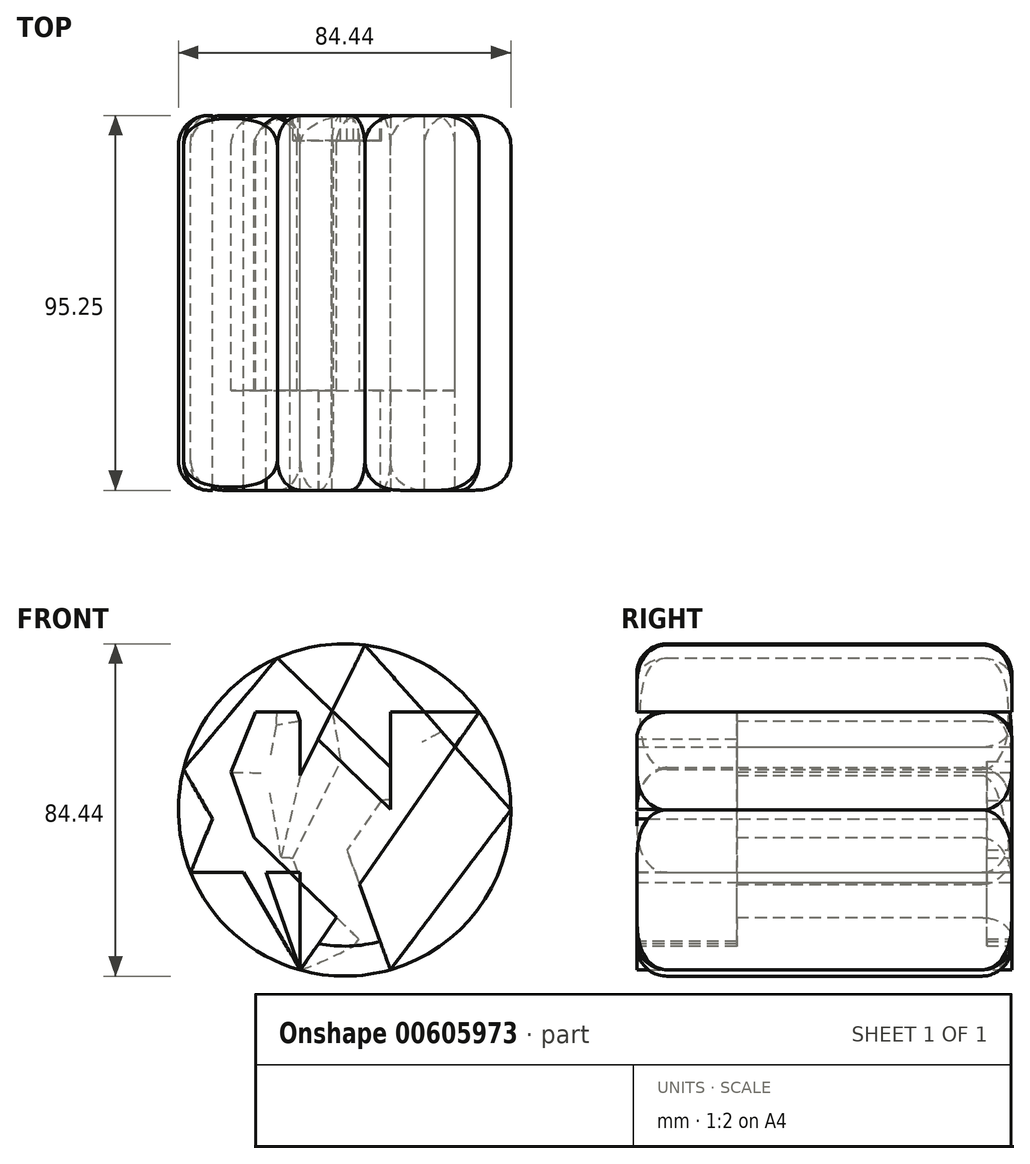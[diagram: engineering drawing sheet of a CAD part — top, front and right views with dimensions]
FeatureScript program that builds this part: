
annotation { "Feature Type Name" : "Feature", "Feature Type Description" : "" }
export const myFeature = defineFeature(function(context is Context, id is Id, definition is map)
    precondition{}
    {
        {
            var Q0;
            Q0=qCreatedBy(makeId("Front.planeOp"),FACE);
            var sketch = newSketch(context, id + "F0", { "sketchPlane" : qUnion([Q0])});
            skCircle(sketch, "E0", {"center": v(0, 0) * mm, "radius": 42.22 * mm});
            skLineSegment(sketch, "E1", {"start": v(-11.28, 40.69) * mm, "end": v(-11.28, -40.69) * mm});
            skLineSegment(sketch, "E2", {"start": v(-11.28, -40.69) * mm, "end": v(-34.14, 24.85) * mm});
            skLineSegment(sketch, "E3", {"start": v(-34.14, 24.85) * mm, "end": v(34.14, 24.85) * mm});
            skLineSegment(sketch, "E4", {"start": v(34.14, 24.85) * mm, "end": v(-11.28, -40.69) * mm});
            skLineSegment(sketch, "E5", {"start": v(11.62, 40.6) * mm, "end": v(11.62, -40.6) * mm});
            skLineSegment(sketch, "E6", {"start": v(11.62, -40.6) * mm, "end": v(-17.09, 38.6) * mm});
            skLineSegment(sketch, "E7", {"start": v(-17.09, 38.6) * mm, "end": v(39.12, -15.88) * mm});
            skLineSegment(sketch, "E8", {"start": v(39.12, -15.88) * mm, "end": v(-39.12, -15.88) * mm});
            skLineSegment(sketch, "E9", {"start": v(-39.12, -15.88) * mm, "end": v(-17.09, 38.6) * mm});
            skLineSegment(sketch, "E10", {"start": v(-30.23, -29.47) * mm, "end": v(5.13, 41.9) * mm});
            skLineSegment(sketch, "E11", {"start": v(5.13, 41.9) * mm, "end": v(42.22, 0) * mm});
            skLineSegment(sketch, "E12", {"start": v(42.22, 0) * mm, "end": v(11.62, -40.6) * mm});
            skLineSegment(sketch, "E13", {"start": v(11.62, -40.6) * mm, "end": v(-40.93, 10.35) * mm});
            skLineSegment(sketch, "E14", {"start": v(-40.93, 10.35) * mm, "end": v(-17.09, 38.6) * mm});
            skLineSegment(sketch, "E15", {"start": v(-40.93, 10.35) * mm, "end": v(-11.28, -40.69) * mm});
            skSolve(sketch);
        }
        {
            var Q0;
            {var subQ0=sQuery(id+"F0.wireOp",EDGE,"E1");var subQ1=sQuery(id+"F0.wireOp",EDGE,"E0");var subQ2=makeQuery(id+"F0.imprint","INTERSECT",VERTEX,{"derivedFrom":[subQ1,subQ0]});Q0=makeQuery(id+"F0.imprint","IMPRINT",FACE,{"disambiguationData":[TD([[makeQuery(id+"F0.imprint","IMPRINT",EDGE,{"disambiguationData":[TD([[subQ2,-1.0]])],"derivedFrom":subQ0}),1.0]])]});}
            var Q1;
            {var subQ0=sQuery(id+"F0.wireOp",EDGE,"E5");var subQ1=sQuery(id+"F0.wireOp",EDGE,"E0");var subQ2=makeQuery(id+"F0.imprint","INTERSECT",VERTEX,{"derivedFrom":[subQ1,subQ0]});Q1=makeQuery(id+"F0.imprint","IMPRINT",FACE,{"disambiguationData":[TD([[makeQuery(id+"F0.imprint","IMPRINT",EDGE,{"disambiguationData":[TD([[subQ2,-1.0]])],"derivedFrom":subQ0}),-1.0]])]});}
            var Q2;
            {var subQ1=sQuery(id+"F0.wireOp",EDGE,"E0");var subQ3=sQuery(id+"F0.wireOp",EDGE,"E5");var subQ4=makeQuery(id+"F0.imprint","INTERSECT",VERTEX,{"derivedFrom":[subQ1,subQ3]});Q2=makeQuery(id+"F0.imprint","IMPRINT",FACE,{"disambiguationData":[TD([[makeQuery(id+"F0.imprint","IMPRINT",EDGE,{"disambiguationData":[TD([[subQ4,-1.0]])],"derivedFrom":subQ3}),1.0]])]});}
            var Q3;
            {var subQ0=sQuery(id+"F0.wireOp",EDGE,"E4");var subQ3=sQuery(id+"F0.wireOp",EDGE,"E11");var subQ5=makeQuery(id+"F0.imprint","INTERSECT",VERTEX,{"derivedFrom":[subQ0,subQ3]});Q3=makeQuery(id+"F0.imprint","IMPRINT",FACE,{"disambiguationData":[TD([[makeQuery(id+"F0.imprint","IMPRINT",EDGE,{"disambiguationData":[TD([[subQ5,1.0]])],"derivedFrom":subQ0}),1.0]])]});}
            var Q4;
            {var subQ0=sQuery(id+"F0.wireOp",EDGE,"E7");var subQ3=sQuery(id+"F0.wireOp",EDGE,"E12");var subQ5=makeQuery(id+"F0.imprint","INTERSECT",VERTEX,{"derivedFrom":[subQ0,subQ3]});Q4=makeQuery(id+"F0.imprint","IMPRINT",FACE,{"disambiguationData":[TD([[makeQuery(id+"F0.imprint","IMPRINT",EDGE,{"disambiguationData":[TD([[subQ5,-1.0]])],"derivedFrom":subQ0}),1.0]])]});}
            var Q5;
            {var subQ1=sQuery(id+"F0.wireOp",EDGE,"E7");var subQ3=sQuery(id+"F0.wireOp",EDGE,"E12");var subQ4=makeQuery(id+"F0.imprint","INTERSECT",VERTEX,{"derivedFrom":[subQ1,subQ3]});Q5=makeQuery(id+"F0.imprint","IMPRINT",FACE,{"disambiguationData":[TD([[makeQuery(id+"F0.imprint","IMPRINT",EDGE,{"disambiguationData":[TD([[subQ4,-1.0]])],"derivedFrom":subQ3}),1.0]])]});}
            var Q6;
            {var subQ0=sQuery(id+"F0.wireOp",EDGE,"E12");var subQ3=sQuery(id+"F0.wireOp",EDGE,"E8");var subQ5=makeQuery(id+"F0.imprint","INTERSECT",VERTEX,{"derivedFrom":[subQ3,subQ0]});Q6=makeQuery(id+"F0.imprint","IMPRINT",FACE,{"disambiguationData":[TD([[makeQuery(id+"F0.imprint","IMPRINT",EDGE,{"disambiguationData":[TD([[subQ5,1.0]])],"derivedFrom":subQ3}),1.0]])]});}
            var Q7;
            {var subQ0=sQuery(id+"F0.wireOp",EDGE,"E4");var subQ3=sQuery(id+"F0.wireOp",EDGE,"E13");var subQ5=makeQuery(id+"F0.imprint","INTERSECT",VERTEX,{"derivedFrom":[subQ0,subQ3]});Q7=makeQuery(id+"F0.imprint","IMPRINT",FACE,{"disambiguationData":[TD([[makeQuery(id+"F0.imprint","IMPRINT",EDGE,{"disambiguationData":[TD([[subQ5,-1.0]])],"derivedFrom":subQ0}),1.0]])]});}
            var Q8;
            {var subQ1=sQuery(id+"F0.wireOp",EDGE,"E0");var subQ3=sQuery(id+"F0.wireOp",EDGE,"E10");var subQ4=makeQuery(id+"F0.imprint","INTERSECT",VERTEX,{"derivedFrom":[subQ1,subQ3]});Q8=makeQuery(id+"F0.imprint","IMPRINT",FACE,{"disambiguationData":[TD([[makeQuery(id+"F0.imprint","IMPRINT",EDGE,{"disambiguationData":[TD([[subQ4,-1.0]])],"derivedFrom":subQ3}),-1.0]])]});}
            var Q9;
            {var subQ1=sQuery(id+"F0.wireOp",EDGE,"E0");var subQ3=sQuery(id+"F0.wireOp",EDGE,"E10");var subQ4=makeQuery(id+"F0.imprint","INTERSECT",VERTEX,{"derivedFrom":[subQ1,subQ3]});Q9=makeQuery(id+"F0.imprint","IMPRINT",FACE,{"disambiguationData":[TD([[makeQuery(id+"F0.imprint","IMPRINT",EDGE,{"disambiguationData":[TD([[subQ4,-1.0]])],"derivedFrom":subQ3}),1.0]])]});}
            var Q10;
            {var subQ0=sQuery(id+"F0.wireOp",EDGE,"E9");var subQ3=sQuery(id+"F0.wireOp",EDGE,"E15");var subQ5=makeQuery(id+"F0.imprint","INTERSECT",VERTEX,{"derivedFrom":[subQ0,subQ3]});Q10=makeQuery(id+"F0.imprint","IMPRINT",FACE,{"disambiguationData":[TD([[makeQuery(id+"F0.imprint","IMPRINT",EDGE,{"disambiguationData":[TD([[subQ5,1.0]])],"derivedFrom":subQ0}),1.0]])]});}
            var Q11;
            {var subQ0=sQuery(id+"F0.wireOp",EDGE,"E2");var subQ3=sQuery(id+"F0.wireOp",EDGE,"E14");var subQ5=makeQuery(id+"F0.imprint","INTERSECT",VERTEX,{"derivedFrom":[subQ0,subQ3]});Q11=makeQuery(id+"F0.imprint","IMPRINT",FACE,{"disambiguationData":[TD([[makeQuery(id+"F0.imprint","IMPRINT",EDGE,{"disambiguationData":[TD([[subQ5,-1.0]])],"derivedFrom":subQ0}),1.0]])]});}
            var Q12;
            {var subQ0=sQuery(id+"F0.wireOp",EDGE,"E1");var subQ1=sQuery(id+"F0.wireOp",EDGE,"E0");var subQ2=makeQuery(id+"F0.imprint","INTERSECT",VERTEX,{"derivedFrom":[subQ1,subQ0]});Q12=makeQuery(id+"F0.imprint","IMPRINT",FACE,{"disambiguationData":[TD([[makeQuery(id+"F0.imprint","IMPRINT",EDGE,{"disambiguationData":[TD([[subQ2,-1.0]])],"derivedFrom":subQ0}),-1.0]])]});}
            var Q13;
            {var subQ1=sQuery(id+"F0.wireOp",EDGE,"E2");var subQ3=sQuery(id+"F0.wireOp",EDGE,"E14");var subQ4=makeQuery(id+"F0.imprint","INTERSECT",VERTEX,{"derivedFrom":[subQ1,subQ3]});Q13=makeQuery(id+"F0.imprint","IMPRINT",FACE,{"disambiguationData":[TD([[makeQuery(id+"F0.imprint","IMPRINT",EDGE,{"disambiguationData":[TD([[subQ4,-1.0]])],"derivedFrom":subQ3}),1.0]])]});}
            var Q14;
            {var subQ0=sQuery(id+"F0.wireOp",EDGE,"E3");var subQ3=sQuery(id+"F0.wireOp",EDGE,"E14");var subQ5=makeQuery(id+"F0.imprint","INTERSECT",VERTEX,{"derivedFrom":[subQ0,subQ3]});Q14=makeQuery(id+"F0.imprint","IMPRINT",FACE,{"disambiguationData":[TD([[makeQuery(id+"F0.imprint","IMPRINT",EDGE,{"disambiguationData":[TD([[subQ5,1.0]])],"derivedFrom":subQ0}),1.0]])]});}
            var Q15;
            {var subQ0=sQuery(id+"F0.wireOp",EDGE,"E10");var subQ1=sQuery(id+"F0.wireOp",EDGE,"E1");var subQ2=makeQuery(id+"F0.imprint","INTERSECT",VERTEX,{"derivedFrom":[subQ1,subQ0]});Q15=makeQuery(id+"F0.imprint","IMPRINT",FACE,{"disambiguationData":[TD([[makeQuery(id+"F0.imprint","IMPRINT",EDGE,{"disambiguationData":[TD([[subQ2,-1.0]])],"derivedFrom":subQ1}),1.0]])]});}
            var Q16;
            {var subQ0=sQuery(id+"F0.wireOp",EDGE,"E10");var subQ1=sQuery(id+"F0.wireOp",EDGE,"E1");var subQ2=makeQuery(id+"F0.imprint","INTERSECT",VERTEX,{"derivedFrom":[subQ1,subQ0]});Q16=makeQuery(id+"F0.imprint","IMPRINT",FACE,{"disambiguationData":[TD([[makeQuery(id+"F0.imprint","IMPRINT",EDGE,{"disambiguationData":[TD([[subQ2,-1.0]])],"derivedFrom":subQ1}),-1.0]])]});}
            var Q17;
            {var subQ0=sQuery(id+"F0.wireOp",EDGE,"E7");var subQ1=sQuery(id+"F0.wireOp",EDGE,"E4");var subQ2=makeQuery(id+"F0.imprint","INTERSECT",VERTEX,{"derivedFrom":[subQ1,subQ0]});Q17=makeQuery(id+"F0.imprint","IMPRINT",FACE,{"disambiguationData":[TD([[makeQuery(id+"F0.imprint","IMPRINT",EDGE,{"disambiguationData":[TD([[subQ2,-1.0]])],"derivedFrom":subQ1}),-1.0]])]});}
            var Q18;
            {var subQ0=sQuery(id+"F0.wireOp",EDGE,"E8");var subQ1=sQuery(id+"F0.wireOp",EDGE,"E4");var subQ2=makeQuery(id+"F0.imprint","INTERSECT",VERTEX,{"derivedFrom":[subQ1,subQ0]});Q18=makeQuery(id+"F0.imprint","IMPRINT",FACE,{"disambiguationData":[TD([[makeQuery(id+"F0.imprint","IMPRINT",EDGE,{"disambiguationData":[TD([[subQ2,-1.0]])],"derivedFrom":subQ1}),-1.0]])]});}
            var Q19;
            {var subQ3=sQuery(id+"F0.wireOp",EDGE,"E10");var subQ11=sQuery(id+"F0.wireOp",EDGE,"E3");var subQ12=makeQuery(id+"F0.imprint","INTERSECT",VERTEX,{"derivedFrom":[subQ11,subQ3]});Q19=makeQuery(id+"F0.imprint","IMPRINT",FACE,{"disambiguationData":[TD([[makeQuery(id+"F0.imprint","IMPRINT",EDGE,{"disambiguationData":[TD([[subQ12,-1.0]])],"derivedFrom":subQ11}),-1.0]])]});}
            var Q20;
            {var subQ0=sQuery(id+"F0.wireOp",EDGE,"E2");var subQ5=sQuery(id+"F0.wireOp",EDGE,"E8");var subQ7=makeQuery(id+"F0.imprint","INTERSECT",VERTEX,{"derivedFrom":[subQ0,subQ5]});Q20=makeQuery(id+"F0.imprint","IMPRINT",FACE,{"disambiguationData":[TD([[makeQuery(id+"F0.imprint","IMPRINT",EDGE,{"disambiguationData":[TD([[subQ7,1.0]])],"derivedFrom":subQ5}),1.0]])]});}
            var Q21;
            {var subQ3=sQuery(id+"F0.wireOp",EDGE,"E8");var subQ6=sQuery(id+"F0.wireOp",EDGE,"E1");var subQ9=makeQuery(id+"F0.imprint","INTERSECT",VERTEX,{"derivedFrom":[subQ6,subQ3]});Q21=makeQuery(id+"F0.imprint","IMPRINT",FACE,{"disambiguationData":[TD([[makeQuery(id+"F0.imprint","IMPRINT",EDGE,{"disambiguationData":[TD([[subQ9,-1.0]])],"derivedFrom":subQ6}),1.0]])]});}
            var Q22;
            {var subQ0=sQuery(id+"F0.wireOp",EDGE,"E6");var subQ1=sQuery(id+"F0.wireOp",EDGE,"E4");var subQ2=makeQuery(id+"F0.imprint","INTERSECT",VERTEX,{"derivedFrom":[subQ1,subQ0]});Q22=makeQuery(id+"F0.imprint","IMPRINT",FACE,{"disambiguationData":[TD([[makeQuery(id+"F0.imprint","IMPRINT",EDGE,{"disambiguationData":[TD([[subQ2,-1.0]])],"derivedFrom":subQ1}),1.0]])]});}
            var Q23;
            {var subQ0=sQuery(id+"F0.wireOp",EDGE,"E5");var subQ1=sQuery(id+"F0.wireOp",EDGE,"E3");var subQ2=makeQuery(id+"F0.imprint","INTERSECT",VERTEX,{"derivedFrom":[subQ1,subQ0]});Q23=makeQuery(id+"F0.imprint","IMPRINT",FACE,{"disambiguationData":[TD([[makeQuery(id+"F0.imprint","IMPRINT",EDGE,{"disambiguationData":[TD([[subQ2,-1.0]])],"derivedFrom":subQ1}),-1.0]])]});}
            var Q24;
            {var subQ0=sQuery(id+"F0.wireOp",EDGE,"E6");var subQ1=sQuery(id+"F0.wireOp",EDGE,"E1");var subQ2=makeQuery(id+"F0.imprint","INTERSECT",VERTEX,{"derivedFrom":[subQ1,subQ0]});Q24=makeQuery(id+"F0.imprint","IMPRINT",FACE,{"disambiguationData":[TD([[makeQuery(id+"F0.imprint","IMPRINT",EDGE,{"disambiguationData":[TD([[subQ2,-1.0]])],"derivedFrom":subQ1}),-1.0]])]});}
            extrude(context, id + "F1", {"entities" : qUnion([Q0, Q1, Q2, Q3, Q4, Q5, Q6, Q7, Q8, Q9, Q10, Q11, Q12, Q13, Q14, Q15, Q16, Q17, Q18, Q19, Q20, Q21, Q22, Q23, Q24]), "depth" : 76.2 * mm, "offsetDistance" : 25.4 * mm, "hasSecondDirection" : true, "secondDirectionOppositeDirection" : true, "secondDirectionDepth" : 19.05 * mm});
        }
        {
            var Q0;
            {var subQ0=sQuery(id+"F0.wireOp",EDGE,"E0");var subQ1=makeQuery(id+"F0.imprint","INTERSECT",VERTEX,{"derivedFrom":[subQ0,sQuery(id+"F0.wireOp",EDGE,"E5")]});Q0=makeQuery(id+"F1.opExtrude","CAP_EDGE",EDGE,{"disambiguationData":[OSD([subQ0]),TDD([makeQuery(id+"F0.imprint","IMPRINT",EDGE,{"disambiguationData":[TD([[subQ1,1.0]])],"derivedFrom":subQ0}),makeQuery(id+"F0.imprint","IMPRINT",EDGE,{"disambiguationData":[TD([[subQ1,-1.0]])],"derivedFrom":subQ0})])],"isStart":false});}
            var Q1;
            {var subQ0=sQuery(id+"F0.wireOp",EDGE,"E0");var subQ1=makeQuery(id+"F0.imprint","INTERSECT",VERTEX,{"derivedFrom":[subQ0,sQuery(id+"F0.wireOp",EDGE,"E1")]});Q1=makeQuery(id+"F1.opExtrude","CAP_EDGE",EDGE,{"disambiguationData":[OSD([subQ0]),TDD([makeQuery(id+"F0.imprint","IMPRINT",EDGE,{"disambiguationData":[TD([[subQ1,1.0]])],"derivedFrom":subQ0}),makeQuery(id+"F0.imprint","IMPRINT",EDGE,{"disambiguationData":[TD([[subQ1,-1.0]])],"derivedFrom":subQ0})])],"isStart":false});}
            var Q2;
            {var subQ0=sQuery(id+"F0.wireOp",EDGE,"E0");var subQ1=makeQuery(id+"F0.imprint","INTERSECT",VERTEX,{"derivedFrom":[subQ0,sQuery(id+"F0.wireOp",EDGE,"E2"),sQuery(id+"F0.wireOp",EDGE,"E3")]});Q2=makeQuery(id+"F1.opExtrude","CAP_EDGE",EDGE,{"disambiguationData":[OSD([subQ0]),TDD([makeQuery(id+"F0.imprint","IMPRINT",EDGE,{"disambiguationData":[TD([[subQ1,1.0]])],"derivedFrom":subQ0}),makeQuery(id+"F0.imprint","IMPRINT",EDGE,{"disambiguationData":[TD([[subQ1,-1.0]])],"derivedFrom":subQ0})])],"isStart":false});}
            var Q3;
            {var subQ0=sQuery(id+"F0.wireOp",EDGE,"E0");Q3=makeQuery(id+"F1.opExtrude","CAP_EDGE",EDGE,{"disambiguationData":[OSD([subQ0]),TDD([makeQuery(id+"F0.imprint","IMPRINT",EDGE,{"disambiguationData":[TD([[makeQuery(id+"F0.imprint","INTERSECT",VERTEX,{"derivedFrom":[subQ0,sQuery(id+"F0.wireOp",EDGE,"E8"),sQuery(id+"F0.wireOp",EDGE,"E9")]}),1.0]])],"derivedFrom":subQ0})])],"isStart":false});}
            var Q4;
            {var subQ0=sQuery(id+"F0.wireOp",EDGE,"E0");var subQ1=makeQuery(id+"F0.imprint","INTERSECT",VERTEX,{"derivedFrom":[subQ0,sQuery(id+"F0.wireOp",EDGE,"E10")]});Q4=makeQuery(id+"F1.opExtrude","CAP_EDGE",EDGE,{"disambiguationData":[OSD([subQ0]),TDD([makeQuery(id+"F0.imprint","IMPRINT",EDGE,{"disambiguationData":[TD([[subQ1,1.0]])],"derivedFrom":subQ0}),makeQuery(id+"F0.imprint","IMPRINT",EDGE,{"disambiguationData":[TD([[subQ1,-1.0]])],"derivedFrom":subQ0})])],"isStart":false});}
            var Q5;
            {var subQ0=sQuery(id+"F0.wireOp",EDGE,"E0");Q5=makeQuery(id+"F1.opExtrude","CAP_EDGE",EDGE,{"disambiguationData":[OSD([subQ0]),TDD([makeQuery(id+"F0.imprint","IMPRINT",EDGE,{"disambiguationData":[TD([[makeQuery(id+"F0.imprint","INTERSECT",VERTEX,{"derivedFrom":[subQ0,sQuery(id+"F0.wireOp",EDGE,"E1"),sQuery(id+"F0.wireOp",EDGE,"E2"),sQuery(id+"F0.wireOp",EDGE,"E4"),sQuery(id+"F0.wireOp",EDGE,"E15")]}),-1.0]])],"derivedFrom":subQ0})])],"isStart":false});}
            var Q6;
            {var subQ0=sQuery(id+"F0.wireOp",EDGE,"E0");var subQ1=makeQuery(id+"F0.imprint","INTERSECT",VERTEX,{"derivedFrom":[subQ0,sQuery(id+"F0.wireOp",EDGE,"E7"),sQuery(id+"F0.wireOp",EDGE,"E8")]});Q6=makeQuery(id+"F1.opExtrude","CAP_EDGE",EDGE,{"disambiguationData":[OSD([subQ0]),TDD([makeQuery(id+"F0.imprint","IMPRINT",EDGE,{"disambiguationData":[TD([[subQ1,1.0]])],"derivedFrom":subQ0}),makeQuery(id+"F0.imprint","IMPRINT",EDGE,{"disambiguationData":[TD([[subQ1,-1.0]])],"derivedFrom":subQ0})])],"isStart":false});}
            var Q7;
            {var subQ0=sQuery(id+"F0.wireOp",EDGE,"E0");Q7=makeQuery(id+"F1.opExtrude","CAP_EDGE",EDGE,{"disambiguationData":[OSD([subQ0]),TDD([makeQuery(id+"F0.imprint","IMPRINT",EDGE,{"disambiguationData":[TD([[makeQuery(id+"F0.imprint","INTERSECT",VERTEX,{"derivedFrom":[subQ0,sQuery(id+"F0.wireOp",EDGE,"E3"),sQuery(id+"F0.wireOp",EDGE,"E4")]}),1.0]])],"derivedFrom":subQ0})])],"isStart":false});}
            var Q8;
            {var subQ0=sQuery(id+"F0.wireOp",EDGE,"E0");var subQ1=makeQuery(id+"F0.imprint","INTERSECT",VERTEX,{"derivedFrom":[subQ0,sQuery(id+"F0.wireOp",EDGE,"E5")]});Q8=makeQuery(id+"F1.opExtrude","CAP_EDGE",EDGE,{"disambiguationData":[OSD([subQ0]),TDD([makeQuery(id+"F0.imprint","IMPRINT",EDGE,{"disambiguationData":[TD([[subQ1,1.0]])],"derivedFrom":subQ0}),makeQuery(id+"F0.imprint","IMPRINT",EDGE,{"disambiguationData":[TD([[subQ1,-1.0]])],"derivedFrom":subQ0})])],"isStart":true});}
            var Q9;
            {var subQ0=sQuery(id+"F0.wireOp",EDGE,"E0");Q9=makeQuery(id+"F1.opExtrude","CAP_EDGE",EDGE,{"disambiguationData":[OSD([subQ0]),TDD([makeQuery(id+"F0.imprint","IMPRINT",EDGE,{"disambiguationData":[TD([[makeQuery(id+"F0.imprint","INTERSECT",VERTEX,{"derivedFrom":[subQ0,sQuery(id+"F0.wireOp",EDGE,"E3"),sQuery(id+"F0.wireOp",EDGE,"E4")]}),1.0]])],"derivedFrom":subQ0})])],"isStart":true});}
            var Q10;
            {var subQ0=sQuery(id+"F0.wireOp",EDGE,"E0");var subQ1=makeQuery(id+"F0.imprint","INTERSECT",VERTEX,{"derivedFrom":[subQ0,sQuery(id+"F0.wireOp",EDGE,"E7"),sQuery(id+"F0.wireOp",EDGE,"E8")]});Q10=makeQuery(id+"F1.opExtrude","CAP_EDGE",EDGE,{"disambiguationData":[OSD([subQ0]),TDD([makeQuery(id+"F0.imprint","IMPRINT",EDGE,{"disambiguationData":[TD([[subQ1,1.0]])],"derivedFrom":subQ0}),makeQuery(id+"F0.imprint","IMPRINT",EDGE,{"disambiguationData":[TD([[subQ1,-1.0]])],"derivedFrom":subQ0})])],"isStart":true});}
            var Q11;
            {var subQ0=sQuery(id+"F0.wireOp",EDGE,"E0");Q11=makeQuery(id+"F1.opExtrude","CAP_EDGE",EDGE,{"disambiguationData":[OSD([subQ0]),TDD([makeQuery(id+"F0.imprint","IMPRINT",EDGE,{"disambiguationData":[TD([[makeQuery(id+"F0.imprint","INTERSECT",VERTEX,{"derivedFrom":[subQ0,sQuery(id+"F0.wireOp",EDGE,"E1"),sQuery(id+"F0.wireOp",EDGE,"E2"),sQuery(id+"F0.wireOp",EDGE,"E4"),sQuery(id+"F0.wireOp",EDGE,"E15")]}),-1.0]])],"derivedFrom":subQ0})])],"isStart":true});}
            var Q12;
            {var subQ0=sQuery(id+"F0.wireOp",EDGE,"E0");Q12=makeQuery(id+"F1.opExtrude","CAP_EDGE",EDGE,{"disambiguationData":[OSD([subQ0]),TDD([makeQuery(id+"F0.imprint","IMPRINT",EDGE,{"disambiguationData":[TD([[makeQuery(id+"F0.imprint","INTERSECT",VERTEX,{"derivedFrom":[subQ0,sQuery(id+"F0.wireOp",EDGE,"E8"),sQuery(id+"F0.wireOp",EDGE,"E9")]}),1.0]])],"derivedFrom":subQ0})])],"isStart":true});}
            var Q13;
            {var subQ0=sQuery(id+"F0.wireOp",EDGE,"E0");var subQ1=makeQuery(id+"F0.imprint","INTERSECT",VERTEX,{"derivedFrom":[subQ0,sQuery(id+"F0.wireOp",EDGE,"E10")]});Q13=makeQuery(id+"F1.opExtrude","CAP_EDGE",EDGE,{"disambiguationData":[OSD([subQ0]),TDD([makeQuery(id+"F0.imprint","IMPRINT",EDGE,{"disambiguationData":[TD([[subQ1,1.0]])],"derivedFrom":subQ0}),makeQuery(id+"F0.imprint","IMPRINT",EDGE,{"disambiguationData":[TD([[subQ1,-1.0]])],"derivedFrom":subQ0})])],"isStart":true});}
            var Q14;
            {var subQ0=sQuery(id+"F0.wireOp",EDGE,"E0");var subQ1=makeQuery(id+"F0.imprint","INTERSECT",VERTEX,{"derivedFrom":[subQ0,sQuery(id+"F0.wireOp",EDGE,"E2"),sQuery(id+"F0.wireOp",EDGE,"E3")]});Q14=makeQuery(id+"F1.opExtrude","CAP_EDGE",EDGE,{"disambiguationData":[OSD([subQ0]),TDD([makeQuery(id+"F0.imprint","IMPRINT",EDGE,{"disambiguationData":[TD([[subQ1,1.0]])],"derivedFrom":subQ0}),makeQuery(id+"F0.imprint","IMPRINT",EDGE,{"disambiguationData":[TD([[subQ1,-1.0]])],"derivedFrom":subQ0})])],"isStart":true});}
            var Q15;
            {var subQ0=sQuery(id+"F0.wireOp",EDGE,"E0");var subQ1=makeQuery(id+"F0.imprint","INTERSECT",VERTEX,{"derivedFrom":[subQ0,sQuery(id+"F0.wireOp",EDGE,"E1")]});Q15=makeQuery(id+"F1.opExtrude","CAP_EDGE",EDGE,{"disambiguationData":[OSD([subQ0]),TDD([makeQuery(id+"F0.imprint","IMPRINT",EDGE,{"disambiguationData":[TD([[subQ1,1.0]])],"derivedFrom":subQ0}),makeQuery(id+"F0.imprint","IMPRINT",EDGE,{"disambiguationData":[TD([[subQ1,-1.0]])],"derivedFrom":subQ0})])],"isStart":true});}
            var Q16;
            {var subQ0=sQuery(id+"F0.wireOp",EDGE,"E7");Q16=makeQuery(id+"F1.opExtrude","CAP_EDGE",EDGE,{"disambiguationData":[OSD([subQ0]),TDD([makeQuery(id+"F0.imprint","IMPRINT",EDGE,{"disambiguationData":[TD([[makeQuery(id+"F0.imprint","INTERSECT",VERTEX,{"derivedFrom":[sQuery(id+"F0.wireOp",EDGE,"E3"),subQ0]}),-1.0]])],"derivedFrom":subQ0})])],"isStart":true});}
            var Q17;
            {var subQ0=sQuery(id+"F0.wireOp",EDGE,"E10");Q17=makeQuery(id+"F1.opExtrude","CAP_EDGE",EDGE,{"disambiguationData":[OSD([subQ0]),TDD([makeQuery(id+"F0.imprint","IMPRINT",EDGE,{"disambiguationData":[TD([[makeQuery(id+"F0.imprint","INTERSECT",VERTEX,{"derivedFrom":[sQuery(id+"F0.wireOp",EDGE,"E1"),subQ0]}),-1.0]])],"derivedFrom":subQ0}),makeQuery(id+"F0.imprint","IMPRINT",EDGE,{"disambiguationData":[TD([[makeQuery(id+"F0.imprint","INTERSECT",VERTEX,{"derivedFrom":[sQuery(id+"F0.wireOp",EDGE,"E3"),subQ0]}),1.0]])],"derivedFrom":subQ0})])],"isStart":true});}
            var Q18;
            {var subQ0=sQuery(id+"F0.wireOp",EDGE,"E1");Q18=makeQuery(id+"F1.opExtrude","CAP_EDGE",EDGE,{"disambiguationData":[OSD([subQ0]),TDD([makeQuery(id+"F0.imprint","IMPRINT",EDGE,{"disambiguationData":[TD([[makeQuery(id+"F0.imprint","INTERSECT",VERTEX,{"derivedFrom":[subQ0,sQuery(id+"F0.wireOp",EDGE,"E6")]}),-1.0]])],"derivedFrom":subQ0})])],"isStart":true});}
            var Q19;
            {var subQ0=sQuery(id+"F0.wireOp",EDGE,"E6");Q19=makeQuery(id+"F1.opExtrude","CAP_EDGE",EDGE,{"disambiguationData":[OSD([subQ0]),TDD([makeQuery(id+"F0.imprint","IMPRINT",EDGE,{"disambiguationData":[TD([[makeQuery(id+"F0.imprint","INTERSECT",VERTEX,{"derivedFrom":[sQuery(id+"F0.wireOp",EDGE,"E1"),subQ0]}),-1.0]])],"derivedFrom":subQ0})])],"isStart":true});}
            var Q20;
            {var subQ0=sQuery(id+"F0.wireOp",EDGE,"E2");Q20=makeQuery(id+"F1.opExtrude","CAP_EDGE",EDGE,{"disambiguationData":[OSD([subQ0]),TDD([makeQuery(id+"F0.imprint","IMPRINT",EDGE,{"disambiguationData":[TD([[makeQuery(id+"F0.imprint","INTERSECT",VERTEX,{"derivedFrom":[subQ0,sQuery(id+"F0.wireOp",EDGE,"E13")]}),-1.0]])],"derivedFrom":subQ0})])],"isStart":true});}
            var Q21;
            {var subQ0=sQuery(id+"F0.wireOp",EDGE,"E9");Q21=makeQuery(id+"F1.opExtrude","CAP_EDGE",EDGE,{"disambiguationData":[OSD([subQ0]),TDD([makeQuery(id+"F0.imprint","IMPRINT",EDGE,{"disambiguationData":[TD([[makeQuery(id+"F0.imprint","INTERSECT",VERTEX,{"derivedFrom":[sQuery(id+"F0.wireOp",EDGE,"E2"),subQ0]}),-1.0]])],"derivedFrom":subQ0})])],"isStart":true});}
            var Q22;
            {var subQ0=sQuery(id+"F0.wireOp",EDGE,"E4");Q22=makeQuery(id+"F1.opExtrude","CAP_EDGE",EDGE,{"disambiguationData":[OSD([subQ0]),TDD([makeQuery(id+"F0.imprint","IMPRINT",EDGE,{"disambiguationData":[TD([[makeQuery(id+"F0.imprint","INTERSECT",VERTEX,{"derivedFrom":[subQ0,sQuery(id+"F0.wireOp",EDGE,"E13")]}),-1.0]])],"derivedFrom":subQ0})])],"isStart":true});}
            var Q23;
            {var subQ0=sQuery(id+"F0.wireOp",EDGE,"E4");var subQ1=makeQuery(id+"F0.imprint","INTERSECT",VERTEX,{"derivedFrom":[subQ0,sQuery(id+"F0.wireOp",EDGE,"E8")]});var subQ2=makeQuery(id+"F0.imprint","INTERSECT",VERTEX,{"derivedFrom":[subQ0,sQuery(id+"F0.wireOp",EDGE,"E5")]});var subQ3=makeQuery(id+"F0.imprint","INTERSECT",VERTEX,{"derivedFrom":[subQ0,sQuery(id+"F0.wireOp",EDGE,"E7")]});Q23=makeQuery(id+"F1.opExtrude","CAP_EDGE",EDGE,{"disambiguationData":[OSD([subQ0]),TDD([makeQuery(id+"F0.imprint","IMPRINT",EDGE,{"disambiguationData":[TD([[makeQuery(id+"F0.imprint","INTERSECT",VERTEX,{"derivedFrom":[subQ0,sQuery(id+"F0.wireOp",EDGE,"E11")]}),-1.0]])],"derivedFrom":subQ0}),makeQuery(id+"F0.imprint","IMPRINT",EDGE,{"disambiguationData":[TD([[subQ3,-1.0]])],"derivedFrom":subQ0}),makeQuery(id+"F0.imprint","IMPRINT",EDGE,{"disambiguationData":[TD([[subQ2,-1.0]])],"derivedFrom":subQ0}),makeQuery(id+"F0.imprint","IMPRINT",EDGE,{"disambiguationData":[TD([[subQ1,-1.0]])],"derivedFrom":subQ0})])],"isStart":true});}
            var Q24;
            {var subQ0=sQuery(id+"F0.wireOp",EDGE,"E3");Q24=makeQuery(id+"F1.opExtrude","CAP_EDGE",EDGE,{"disambiguationData":[OSD([subQ0]),TDD([makeQuery(id+"F0.imprint","IMPRINT",EDGE,{"disambiguationData":[TD([[makeQuery(id+"F0.imprint","INTERSECT",VERTEX,{"derivedFrom":[subQ0,sQuery(id+"F0.wireOp",EDGE,"E5")]}),-1.0]])],"derivedFrom":subQ0})])],"isStart":true});}
            var Q25;
            {var subQ0=sQuery(id+"F0.wireOp",EDGE,"E7");Q25=makeQuery(id+"F1.opExtrude","CAP_EDGE",EDGE,{"disambiguationData":[OSD([subQ0]),TDD([makeQuery(id+"F0.imprint","IMPRINT",EDGE,{"disambiguationData":[TD([[makeQuery(id+"F0.imprint","INTERSECT",VERTEX,{"derivedFrom":[sQuery(id+"F0.wireOp",EDGE,"E3"),subQ0]}),-1.0]])],"derivedFrom":subQ0})])],"isStart":false});}
            fillet(context, id + "F2", {"entities" : qUnion([Q0, Q1, Q2, Q3, Q4, Q5, Q6, Q7, Q8, Q9, Q10, Q11, Q12, Q13, Q14, Q15, Q16, Q17, Q18, Q19, Q20, Q21, Q22, Q23, Q24, Q25]), "radius" : 7.62 * mm, "tangentPropagation" : true, "allowEdgeOverflow" : false});
        }
        {
            var Q0;
            Q0=makeQuery(id+"F2.opFillet","SPLIT",FACE,{"disambiguationData":[OD(2.0)],"derivedFrom":makeQuery(id+"F1.opExtrude","CAP_FACE",FACE,{"disambiguationData":[OSD([sQuery(id+"F0.wireOp",EDGE,"E0"),sQuery(id+"F0.wireOp",EDGE,"E1"),sQuery(id+"F0.wireOp",EDGE,"E2"),sQuery(id+"F0.wireOp",EDGE,"E3"),sQuery(id+"F0.wireOp",EDGE,"E4"),sQuery(id+"F0.wireOp",EDGE,"E5"),sQuery(id+"F0.wireOp",EDGE,"E6"),sQuery(id+"F0.wireOp",EDGE,"E7"),sQuery(id+"F0.wireOp",EDGE,"E8"),sQuery(id+"F0.wireOp",EDGE,"E9"),sQuery(id+"F0.wireOp",EDGE,"E10"),sQuery(id+"F0.wireOp",EDGE,"E11"),sQuery(id+"F0.wireOp",EDGE,"E13")])],"isStart":true})});
            extrude(context, id + "F3", {"entities" : qUnion([Q0]), "operationType" : NewBodyOperationType.REMOVE, "oppositeDirection" : true, "depth" : 6.35 * mm, "offsetDistance" : 25.4 * mm});
        }
        {
            var Q0;
            Q0=makeQuery(id+"F1.opExtrude","CAP_FACE",FACE,{"disambiguationData":[OSD([sQuery(id+"F0.wireOp",EDGE,"E0"),sQuery(id+"F0.wireOp",EDGE,"E1"),sQuery(id+"F0.wireOp",EDGE,"E2"),sQuery(id+"F0.wireOp",EDGE,"E3"),sQuery(id+"F0.wireOp",EDGE,"E4"),sQuery(id+"F0.wireOp",EDGE,"E5"),sQuery(id+"F0.wireOp",EDGE,"E6"),sQuery(id+"F0.wireOp",EDGE,"E7"),sQuery(id+"F0.wireOp",EDGE,"E8"),sQuery(id+"F0.wireOp",EDGE,"E9"),sQuery(id+"F0.wireOp",EDGE,"E10"),sQuery(id+"F0.wireOp",EDGE,"E11"),sQuery(id+"F0.wireOp",EDGE,"E13")])],"isStart":false});
            extrude(context, id + "F4", {"entities" : qUnion([Q0]), "operationType" : NewBodyOperationType.REMOVE, "oppositeDirection" : true, "depth" : 25.4 * mm, "offsetDistance" : 25.4 * mm});
        }
    });
